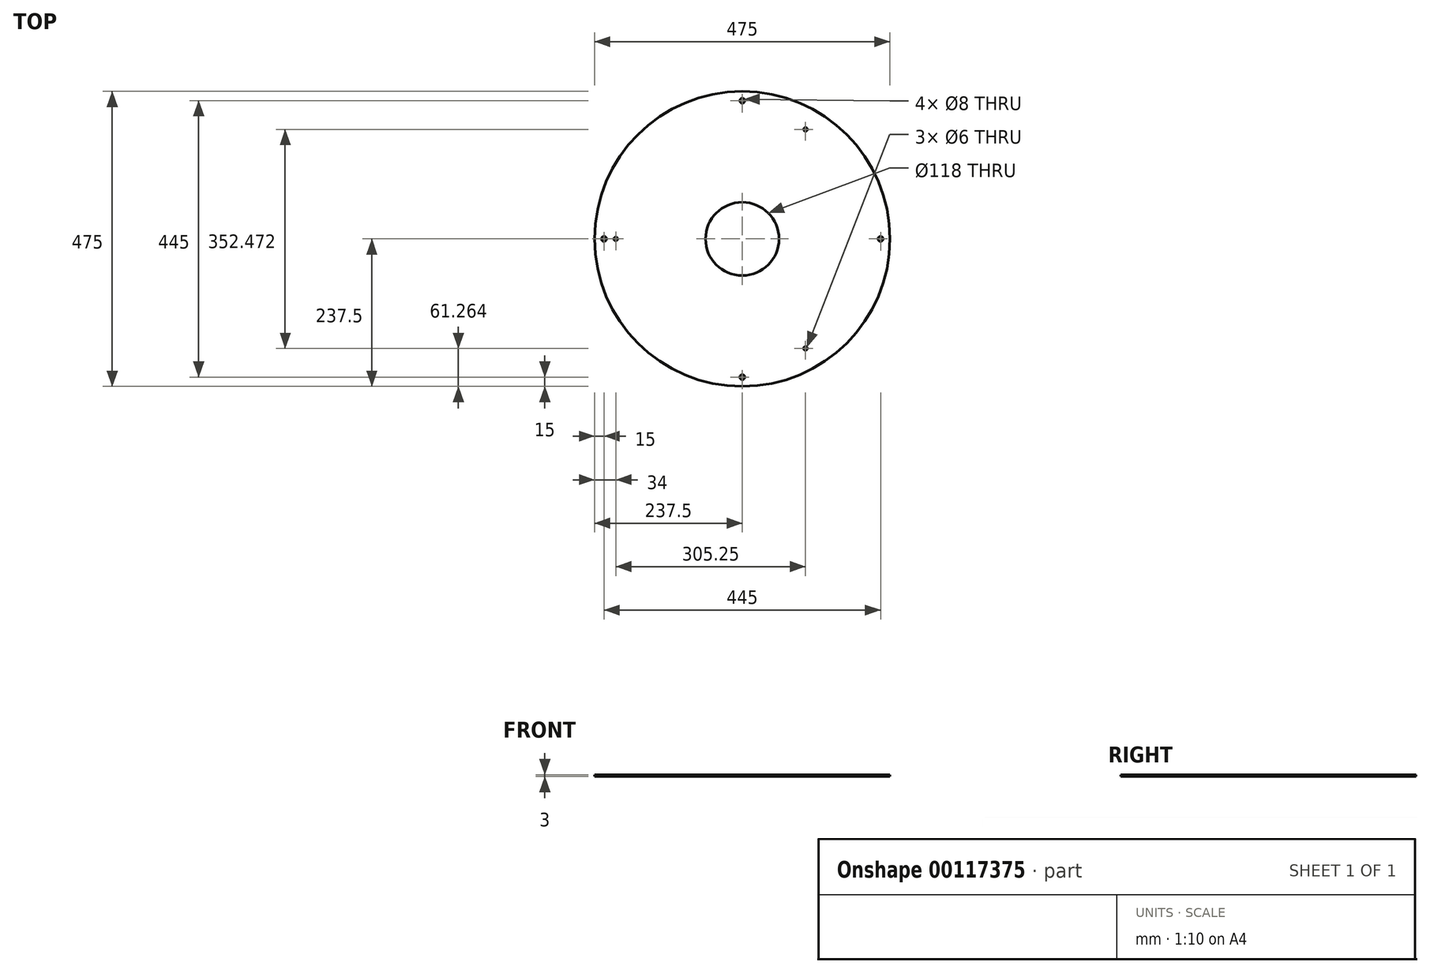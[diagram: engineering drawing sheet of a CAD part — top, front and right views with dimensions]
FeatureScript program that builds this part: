
annotation { "Feature Type Name" : "Feature", "Feature Type Description" : "" }
export const myFeature = defineFeature(function(context is Context, id is Id, definition is map)
    precondition{}
    {
        {
            var Q0;
            Q0=qCreatedBy(makeId("Top.planeOp"),FACE);
            var sketch = newSketch(context, id + "F0", { "sketchPlane" : qUnion([Q0])});
            skCircle(sketch, "E0", {"center": v(0, 0) * mm, "radius": 59 * mm});
            skCircle(sketch, "E1", {"center": v(0, 0) * mm, "radius": 237.5 * mm});
            skPoint(sketch, "E2", {"position": v(222.5, 0) * mm});
            skLineSegment(sketch, "E3", {"start": v(0, 0) * mm, "end": v(222.5, 0) * mm, "construction": true});
            skLineSegment(sketch, "E4", {"start": v(0, 0) * mm, "end": v(0, 104.94) * mm, "construction": true});
            skPoint(sketch, "E5.1.0", {"position": v(0, 222.5) * mm});
            skPoint(sketch, "E5.2.0", {"position": v(-222.5, 0) * mm});
            skPoint(sketch, "E5.3.0", {"position": v(0, -222.5) * mm});
            skCircle(sketch, "E6", {"center": v(0, 0) * mm, "radius": 207.5 * mm, "construction": true});
            skCircle(sketch, "E7", {"center": v(0, 0) * mm, "radius": 203.5 * mm, "construction": true});
            skPoint(sketch, "E8", {"position": v(-203.5, 0) * mm});
            skLineSegment(sketch, "E9", {"start": v(-203.5, 0) * mm, "end": v(0, 0) * mm});
            skPoint(sketch, "E10.1.0", {"position": v(101.75, -176.24) * mm});
            skPoint(sketch, "E10.2.0", {"position": v(101.75, 176.24) * mm});
            skLineSegment(sketch, "E10.anchor1", {"start": v(0, 0) * mm, "end": v(-203.5, 0) * mm, "construction": true});
            skLineSegment(sketch, "E10.anchor2", {"start": v(0, 0) * mm, "end": v(101.75, 176.24) * mm, "construction": true});
            skSolve(sketch);
        }
        {
            var Q0;
            Q0=qSketchRegion(id+"F0",true);
            extrude(context, id + "F1", {"entities" : qUnion([Q0]), "depth" : 3 * mm});
        }
        {
            var Q0;
            Q0=sQuery(id+"F0.wireOp",VERTEX,"E2");
            var Q1;
            Q1=sQuery(id+"F0.wireOp",VERTEX,"E5.1.0");
            var Q2;
            Q2=sQuery(id+"F0.wireOp",VERTEX,"E5.2.0");
            var Q3;
            Q3=sQuery(id+"F0.wireOp",VERTEX,"E5.3.0");
            var Q4;
            Q4=makeQuery(id+"F1.opExtrude","SWEPT_BODY",BODY,{"disambiguationData":[OSD([sQuery(id+"F0.wireOp",EDGE,"E0"),sQuery(id+"F0.wireOp",EDGE,"E1")])]});
            hole(context, id + "F2", {"style" : HoleStyle.SIMPLE, "endStyle" : HoleEndStyle.THROUGH, "oppositeDirection" : true, "holeDiameter" : 8 * mm, "locations" : qUnion([Q0, Q1, Q2, Q3]), "scope" : qUnion([Q4]), "tappedDepth" : 12 * mm, "tapClearance" : 3});
        }
        {
            var Q0;
            Q0=sQuery(id+"F0.wireOp",VERTEX,"E8");
            var Q1;
            Q1=sQuery(id+"F0.wireOp",VERTEX,"E10.2.0");
            var Q2;
            Q2=sQuery(id+"F0.wireOp",VERTEX,"E10.1.0");
            var Q3;
            Q3=makeQuery(id+"F1.opExtrude","SWEPT_BODY",BODY,{"disambiguationData":[OSD([sQuery(id+"F0.wireOp",EDGE,"E0"),sQuery(id+"F0.wireOp",EDGE,"E1")])]});
            hole(context, id + "F3", {"style" : HoleStyle.SIMPLE, "endStyle" : HoleEndStyle.THROUGH, "oppositeDirection" : true, "holeDiameter" : 6 * mm, "tappedDepth" : 12 * mm, "tapClearance" : 3, "locations" : qUnion([Q0, Q1, Q2]), "scope" : qUnion([Q3])});
        }
    });
